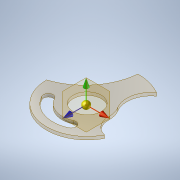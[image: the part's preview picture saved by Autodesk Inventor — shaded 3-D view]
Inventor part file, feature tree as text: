
AUTODESK INVENTOR PART (.ipt)
format: ipt  version: 2020 (Build 240168000, 168)  size: 163,328 bytes
history: native  units: in
note: dims shown in document units (in); Inventor stores cm internally (conversion verified against a paired STEP export)
features: extrude x2, sketch x2
ambient origin geometry x8: Origin, YZ Plane, XZ Plane, XY Plane, X Axis, Y Axis, Z Axis, Center Point
bodies: Solid1 (feature_tree)
feature tree (4):
  extrude  "Extrusion1"  Depth=3.937in
  extrude  "Extrusion3"  Depth=0.1181in
  sketch  "Sketch1"  dims[d0=1.0945in d1=3.937in]
  sketch  "Sketch3"  dims[d2=3.1496in d3=0.315in d4=0.9843in d5=0.315in d6=0.1181in d7=0.0in d10=0.1181in d11=0.0in d12=0.0197in d13=0.0344in d14=0.0197in d15=0.0344in]
